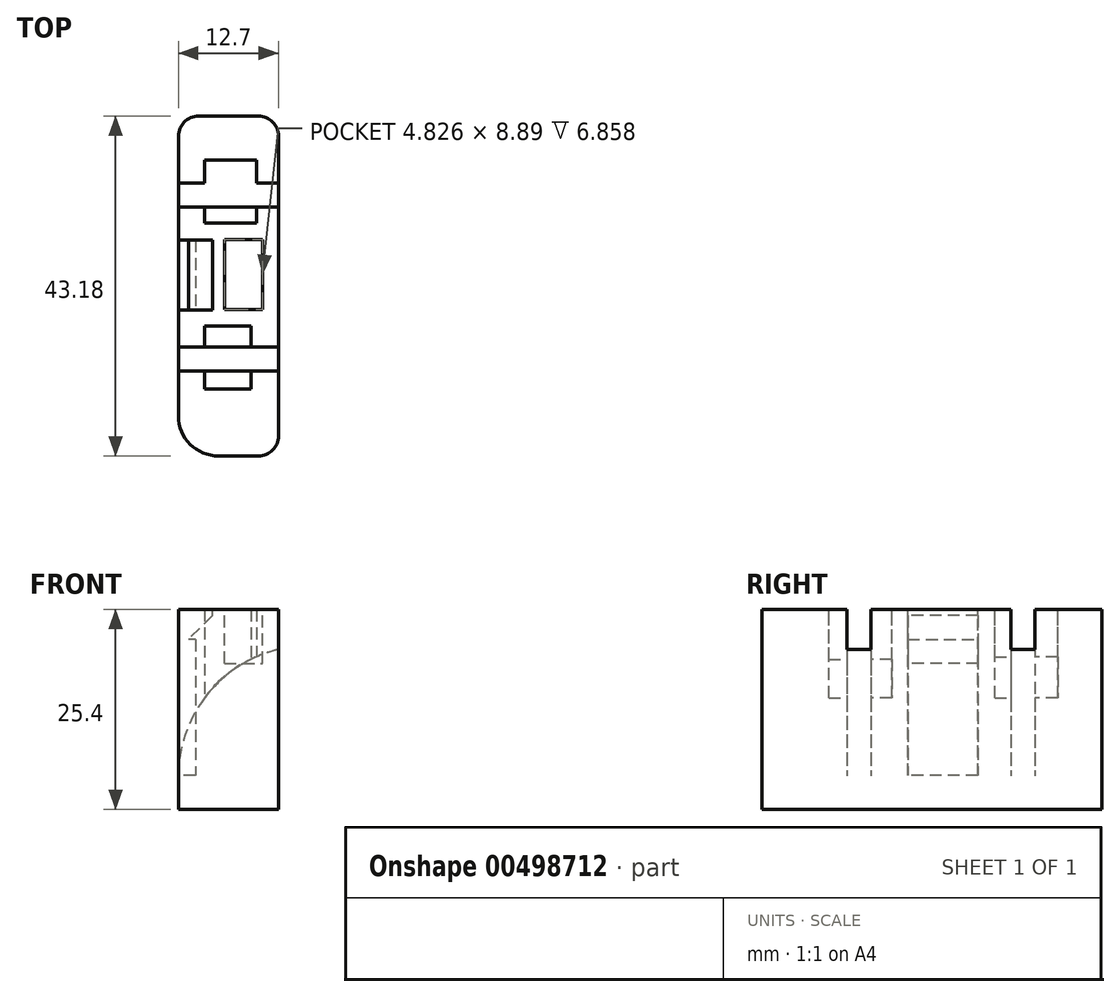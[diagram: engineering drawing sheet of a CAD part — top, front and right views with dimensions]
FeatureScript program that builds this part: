
annotation { "Feature Type Name" : "Feature", "Feature Type Description" : "" }
export const myFeature = defineFeature(function(context is Context, id is Id, definition is map)
    precondition{}
    {
        {
            var Q0;
            Q0=qCreatedBy(makeId("Top.planeOp"),FACE);
            var sketch = newSketch(context, id + "F0", { "sketchPlane" : qUnion([Q0])});
            skLineSegment(sketch, "E0.bottom", {"start": v(3.8, 21.6) * mm, "end": v(-3.81, 21.6) * mm});
            skLineSegment(sketch, "E0.top", {"start": v(3.8, -21.59) * mm, "end": v(-1.27, -21.59) * mm});
            skLineSegment(sketch, "E0.left", {"start": v(6.35, 19.05) * mm, "end": v(6.35, -19.05) * mm});
            skLineSegment(sketch, "E0.right", {"start": v(-6.35, 19.05) * mm, "end": v(-6.35, -16.51) * mm});
            skPoint(sketch, "E0.middle", {"position": v(0, 0) * mm});
            skPoint(sketch, "E1.visualSharp", {"position": v(6.35, 21.6) * mm});
            skArc(sketch, "E1.filletArc", {"start": v(6.35, 19.05) * mm, "mid": v(5.6, 20.85) * mm, "end": v(3.8, 21.6) * mm});
            skPoint(sketch, "E2.visualSharp", {"position": v(-6.35, 21.6) * mm});
            skArc(sketch, "E2.filletArc", {"start": v(-3.81, 21.59) * mm, "mid": v(-5.6, 20.85) * mm, "end": v(-6.35, 19.05) * mm});
            skPoint(sketch, "E3.visualSharp", {"position": v(6.35, -21.59) * mm});
            skArc(sketch, "E3.filletArc", {"start": v(3.8, -21.59) * mm, "mid": v(5.6, -20.85) * mm, "end": v(6.35, -19.05) * mm});
            skPoint(sketch, "E4.visualSharp", {"position": v(-6.35, -21.59) * mm});
            skArc(sketch, "E4.filletArc", {"start": v(-6.35, -16.51) * mm, "mid": v(-4.86, -20.1) * mm, "end": v(-1.27, -21.59) * mm});
            skSolve(sketch);
        }
        {
            var Q0;
            Q0 = qSketchRegion(id + "F0", true);
            extrude(context, id + "F1", {"entities" : qUnion([Q0]), "depth" : 25.4 * mm});
        }
        {
            var Q0;
            Q0=makeQuery(id+"F1.opExtrude","SWEPT_FACE",FACE,{"disambiguationData":[OSD([sQuery(id+"F0.wireOp",EDGE,"E0.left")])]});
            var sketch = newSketch(context, id + "F2", { "sketchPlane" : qUnion([Q0])});
            skLineSegment(sketch, "E5.bottom", {"start": v(-10.8, 25.4) * mm, "end": v(-7.75, 25.4) * mm});
            skLineSegment(sketch, "E5.top", {"start": v(-10.8, 20.32) * mm, "end": v(-7.75, 20.32) * mm});
            skLineSegment(sketch, "E5.left", {"start": v(-10.8, 25.4) * mm, "end": v(-10.8, 20.32) * mm});
            skLineSegment(sketch, "E5.right", {"start": v(-7.75, 25.4) * mm, "end": v(-7.75, 20.32) * mm});
            skLineSegment(sketch, "E6.bottom", {"start": v(10.03, 25.4) * mm, "end": v(13.08, 25.4) * mm});
            skLineSegment(sketch, "E6.top", {"start": v(10.03, 20.32) * mm, "end": v(13.08, 20.32) * mm});
            skLineSegment(sketch, "E6.left", {"start": v(10.03, 25.4) * mm, "end": v(10.03, 20.32) * mm});
            skLineSegment(sketch, "E6.right", {"start": v(13.08, 25.4) * mm, "end": v(13.08, 20.32) * mm});
            skSolve(sketch);
        }
        {
            var Q0;
            Q0=makeQuery(id+"F2.imprint","IMPRINT",FACE,{"disambiguationData":[TD([[makeQuery(id+"F2.imprint","IMPRINT",EDGE,{"derivedFrom":sQuery(id+"F2.wireOp",EDGE,"E5.bottom")}),1.0]])]});
            var Q1;
            Q1=makeQuery(id+"F2.imprint","IMPRINT",FACE,{"disambiguationData":[TD([[makeQuery(id+"F2.imprint","IMPRINT",EDGE,{"derivedFrom":sQuery(id+"F2.wireOp",EDGE,"E6.bottom")}),1.0]])]});
            extrude(context, id + "F3", {"entities" : qUnion([Q0, Q1]), "operationType" : NewBodyOperationType.REMOVE, "oppositeDirection" : true, "depth" : 15.24 * mm});
        }
        {
            var Q0;
            Q0=makeQuery(id+"F3.boolean.opBoolean","INTERSECT",EDGE,{"derivedFrom":[makeQuery(id+"F1.opExtrude","SWEPT_FACE",FACE,{"disambiguationData":[OSD([sQuery(id+"F0.wireOp",EDGE,"E0.right")])]}),makeQuery(id+"F3.opExtrude","SWEPT_FACE",FACE,{"disambiguationData":[OSD([sQuery(id+"F2.wireOp",EDGE,"E6.top")])]})]});
            fillet(context, id + "F4", {"entities" : qUnion([Q0]), "radius" : 16.5 * mm, "tangentPropagation" : true, "allowEdgeOverflow" : false});
        }
        {
            var Q0;
            Q0=makeQuery(id+"F3.boolean.opBoolean","INTERSECT",EDGE,{"derivedFrom":[makeQuery(id+"F1.opExtrude","SWEPT_FACE",FACE,{"disambiguationData":[OSD([sQuery(id+"F0.wireOp",EDGE,"E0.right")])]}),makeQuery(id+"F3.opExtrude","SWEPT_FACE",FACE,{"disambiguationData":[OSD([sQuery(id+"F2.wireOp",EDGE,"E5.top")])]})]});
            fillet(context, id + "F5", {"entities" : qUnion([Q0]), "radius" : 16.5 * mm, "tangentPropagation" : true, "allowEdgeOverflow" : false});
        }
        {
            var Q0;
            {var subQ0=sQuery(id+"F0.wireOp",EDGE,"E0.left");var subQ1=sQuery(id+"F0.wireOp",EDGE,"E0.right");Q0=makeQuery(id+"F3.boolean.opBoolean","SPLIT",FACE,{"disambiguationData":[TD([makeQuery(id+"F3.opExtrude","SWEPT_FACE",FACE,{"disambiguationData":[OSD([sQuery(id+"F2.wireOp",EDGE,"E5.right")])]})])],"derivedFrom":makeQuery(id+"F1.opExtrude","CAP_FACE",FACE,{"disambiguationData":[OSD([sQuery(id+"F0.wireOp",EDGE,"E0.bottom"),sQuery(id+"F0.wireOp",EDGE,"E0.top"),subQ0,subQ1,sQuery(id+"F0.wireOp",EDGE,"E1.filletArc"),sQuery(id+"F0.wireOp",EDGE,"E2.filletArc"),sQuery(id+"F0.wireOp",EDGE,"E3.filletArc"),sQuery(id+"F0.wireOp",EDGE,"E4.filletArc")])],"isStart":false})});}
            var sketch = newSketch(context, id + "F6", { "sketchPlane" : qUnion([Q0])});
            skLineSegment(sketch, "E7.bottom", {"start": v(-3.05, -5.08) * mm, "end": v(2.9, -5.08) * mm});
            skLineSegment(sketch, "E7.top", {"start": v(-3.05, -13.08) * mm, "end": v(2.9, -13.08) * mm});
            skLineSegment(sketch, "E7.left", {"start": v(-3.05, -5.08) * mm, "end": v(-3.05, -13.08) * mm});
            skLineSegment(sketch, "E7.right", {"start": v(2.9, -5.08) * mm, "end": v(2.9, -13.08) * mm});
            skLineSegment(sketch, "E8.bottom", {"start": v(-3.05, 16) * mm, "end": v(3.54, 16) * mm});
            skLineSegment(sketch, "E8.top", {"start": v(-3.05, 8) * mm, "end": v(3.54, 8) * mm});
            skLineSegment(sketch, "E8.left", {"start": v(-3.05, 16) * mm, "end": v(-3.05, 8) * mm});
            skLineSegment(sketch, "E8.right", {"start": v(3.54, 16) * mm, "end": v(3.54, 8) * mm});
            skSolve(sketch);
        }
        {
            var Q0;
            {var subQ0=sQuery(id+"F6.wireOp",EDGE,"E8.bottom");Q0=makeQuery(id+"F6.imprint","IMPRINT",FACE,{"disambiguationData":[TD([[makeQuery(id+"F6.imprint","IMPRINT",EDGE,{"derivedFrom":subQ0}),-1.0]])]});}
            var Q1;
            {var subQ0=sQuery(id+"F6.wireOp",EDGE,"E8.top");Q1=makeQuery(id+"F6.imprint","IMPRINT",FACE,{"disambiguationData":[TD([[makeQuery(id+"F6.imprint","IMPRINT",EDGE,{"derivedFrom":subQ0}),1.0]])]});}
            var Q2;
            {var subQ0=sQuery(id+"F6.wireOp",EDGE,"E7.bottom");Q2=makeQuery(id+"F6.imprint","IMPRINT",FACE,{"disambiguationData":[TD([[makeQuery(id+"F6.imprint","IMPRINT",EDGE,{"derivedFrom":subQ0}),-1.0]])]});}
            var Q3;
            {var subQ0=sQuery(id+"F6.wireOp",EDGE,"E7.top");Q3=makeQuery(id+"F6.imprint","IMPRINT",FACE,{"disambiguationData":[TD([[makeQuery(id+"F6.imprint","IMPRINT",EDGE,{"derivedFrom":subQ0}),1.0]])]});}
            extrude(context, id + "F7", {"entities" : qUnion([Q0, Q1, Q2, Q3]), "operationType" : NewBodyOperationType.REMOVE, "oppositeDirection" : true, "depth" : 5.6 * mm});
        }
        {
            var Q0;
            Q0=makeQuery(id+"F3.boolean.opBoolean","COPY",FACE,{"derivedFrom":makeQuery(id+"F3.opExtrude","SWEPT_FACE",FACE,{"disambiguationData":[OSD([sQuery(id+"F2.wireOp",EDGE,"E5.left")])]})});
            var sketch = newSketch(context, id + "F8", { "sketchPlane" : qUnion([Q0])});
            skLineSegment(sketch, "E9", {"start": v(-2.9, 19.81) * mm, "end": v(-2.9, 19.08) * mm});
            skLineSegment(sketch, "E10", {"start": v(3.05, 19.81) * mm, "end": v(3.05, 14.16) * mm});
            skLineSegment(sketch, "E11", {"start": v(-2.9, 19.81) * mm, "end": v(3.05, 19.81) * mm});
            skArc(sketch, "E12", {"start": v(3.05, 14.16) * mm, "mid": v(0.38, 16.99) * mm, "end": v(-2.9, 19.08) * mm});
            skSolve(sketch);
        }
        {
            var Q0;
            Q0=makeQuery(id+"F8.imprint","IMPRINT",FACE,{"disambiguationData":[TD([[makeQuery(id+"F8.imprint","IMPRINT",EDGE,{"derivedFrom":sQuery(id+"F8.wireOp",EDGE,"E9")}),1.0]])]});
            extrude(context, id + "F9", {"entities" : qUnion([Q0]), "operationType" : NewBodyOperationType.REMOVE, "oppositeDirection" : true, "depth" : 2.3 * mm});
        }
        {
            var Q0;
            Q0=makeQuery(id+"F3.boolean.opBoolean","COPY",FACE,{"derivedFrom":makeQuery(id+"F3.opExtrude","SWEPT_FACE",FACE,{"disambiguationData":[OSD([sQuery(id+"F2.wireOp",EDGE,"E5.right")])]})});
            var sketch = newSketch(context, id + "F10", { "sketchPlane" : qUnion([Q0])});
            skLineSegment(sketch, "E13", {"start": v(2.9, 19.81) * mm, "end": v(2.9, 19.08) * mm});
            skLineSegment(sketch, "E14", {"start": v(-3.05, 19.81) * mm, "end": v(-3.05, 14.16) * mm});
            skLineSegment(sketch, "E15", {"start": v(-3.05, 19.81) * mm, "end": v(2.9, 19.81) * mm});
            skArc(sketch, "E16", {"start": v(2.9, 19.08) * mm, "mid": v(-0.38, 16.99) * mm, "end": v(-3.05, 14.16) * mm});
            skSolve(sketch);
        }
        {
            var Q0;
            Q0=makeQuery(id+"F10.imprint","IMPRINT",FACE,{"disambiguationData":[TD([[makeQuery(id+"F10.imprint","IMPRINT",EDGE,{"derivedFrom":sQuery(id+"F10.wireOp",EDGE,"E13")}),-1.0]])]});
            extrude(context, id + "F11", {"entities" : qUnion([Q0]), "operationType" : NewBodyOperationType.REMOVE, "oppositeDirection" : true, "depth" : 2.67 * mm});
        }
        {
            var Q0;
            Q0=makeQuery(id+"F3.boolean.opBoolean","COPY",FACE,{"derivedFrom":makeQuery(id+"F3.opExtrude","SWEPT_FACE",FACE,{"disambiguationData":[OSD([sQuery(id+"F2.wireOp",EDGE,"E6.right")])]})});
            var sketch = newSketch(context, id + "F12", { "sketchPlane" : qUnion([Q0])});
            skLineSegment(sketch, "E17", {"start": v(3.54, 19.81) * mm, "end": v(3.54, 19.38) * mm});
            skLineSegment(sketch, "E18", {"start": v(3.54, 19.81) * mm, "end": v(-3.05, 19.81) * mm});
            skPoint(sketch, "E19.endSnap0", {"position": v(-2.8, 14.5) * mm});
            skLineSegment(sketch, "E20", {"start": v(-3.05, 19.81) * mm, "end": v(-3.05, 14.16) * mm});
            skArc(sketch, "E21", {"start": v(3.54, 19.38) * mm, "mid": v(-0.08, 17.19) * mm, "end": v(-3.05, 14.16) * mm});
            skSolve(sketch);
        }
        {
            var Q0;
            {var subQ0=sQuery(id+"F12.wireOp",EDGE,"E17");Q0=makeQuery(id+"F12.imprint","IMPRINT",FACE,{"disambiguationData":[TD([[makeQuery(id+"F12.imprint","IMPRINT",EDGE,{"derivedFrom":subQ0}),-1.0]])]});}
            extrude(context, id + "F13", {"entities" : qUnion([Q0]), "operationType" : NewBodyOperationType.REMOVE, "oppositeDirection" : true, "depth" : 2.92 * mm});
        }
        {
            var Q0;
            Q0=makeQuery(id+"F3.boolean.opBoolean","COPY",FACE,{"derivedFrom":makeQuery(id+"F3.opExtrude","SWEPT_FACE",FACE,{"disambiguationData":[OSD([sQuery(id+"F2.wireOp",EDGE,"E6.left")])]})});
            var sketch = newSketch(context, id + "F14", { "sketchPlane" : qUnion([Q0])});
            skLineSegment(sketch, "E22", {"start": v(3.05, 19.81) * mm, "end": v(-3.54, 19.81) * mm});
            skLineSegment(sketch, "E23", {"start": v(-3.54, 19.81) * mm, "end": v(-3.54, 19.38) * mm});
            skLineSegment(sketch, "E24", {"start": v(3.05, 19.81) * mm, "end": v(3.05, 14.16) * mm});
            skArc(sketch, "E25", {"start": v(3.05, 14.16) * mm, "mid": v(0.1, 17.21) * mm, "end": v(-3.54, 19.38) * mm});
            skSolve(sketch);
        }
        {
            var Q0;
            Q0=makeQuery(id+"F14.imprint","IMPRINT",FACE,{"disambiguationData":[TD([[makeQuery(id+"F14.imprint","IMPRINT",EDGE,{"derivedFrom":sQuery(id+"F14.wireOp",EDGE,"E22")}),-1.0]])]});
            extrude(context, id + "F15", {"entities" : qUnion([Q0]), "operationType" : NewBodyOperationType.REMOVE, "oppositeDirection" : true, "depth" : 2.03 * mm});
        }
        {
            var Q0;
            {var subQ0=sQuery(id+"F0.wireOp",EDGE,"E0.left");var subQ1=sQuery(id+"F0.wireOp",EDGE,"E0.right");Q0=makeQuery(id+"F3.boolean.opBoolean","SPLIT",FACE,{"disambiguationData":[TD([makeQuery(id+"F3.opExtrude","SWEPT_FACE",FACE,{"disambiguationData":[OSD([sQuery(id+"F2.wireOp",EDGE,"E5.right")])]})])],"derivedFrom":makeQuery(id+"F1.opExtrude","CAP_FACE",FACE,{"disambiguationData":[OSD([sQuery(id+"F0.wireOp",EDGE,"E0.bottom"),sQuery(id+"F0.wireOp",EDGE,"E0.top"),subQ0,subQ1,sQuery(id+"F0.wireOp",EDGE,"E1.filletArc"),sQuery(id+"F0.wireOp",EDGE,"E2.filletArc"),sQuery(id+"F0.wireOp",EDGE,"E3.filletArc"),sQuery(id+"F0.wireOp",EDGE,"E4.filletArc")])],"isStart":false})});}
            var sketch = newSketch(context, id + "F16", { "sketchPlane" : qUnion([Q0])});
            skLineSegment(sketch, "E26.bottom", {"start": v(-0.5, 5.9) * mm, "end": v(4.32, 5.9) * mm});
            skLineSegment(sketch, "E26.top", {"start": v(-0.5, -2.98) * mm, "end": v(4.32, -2.98) * mm});
            skLineSegment(sketch, "E26.left", {"start": v(-0.5, 5.9) * mm, "end": v(-0.5, -2.98) * mm});
            skLineSegment(sketch, "E26.right", {"start": v(4.32, 5.9) * mm, "end": v(4.32, -2.98) * mm});
            skSolve(sketch);
        }
        {
            var Q0;
            Q0=makeQuery(id+"F16.imprint","IMPRINT",FACE,{"disambiguationData":[TD([[makeQuery(id+"F16.imprint","IMPRINT",EDGE,{"derivedFrom":sQuery(id+"F16.wireOp",EDGE,"E26.bottom")}),-1.0]])]});
            extrude(context, id + "F17", {"entities" : qUnion([Q0]), "operationType" : NewBodyOperationType.REMOVE, "oppositeDirection" : true, "depth" : 6.86 * mm});
        }
        {
            var Q0;
            {var subQ0=sQuery(id+"F0.wireOp",EDGE,"E0.left");var subQ1=sQuery(id+"F0.wireOp",EDGE,"E0.right");Q0=makeQuery(id+"F3.boolean.opBoolean","SPLIT",FACE,{"disambiguationData":[TD([makeQuery(id+"F3.opExtrude","SWEPT_FACE",FACE,{"disambiguationData":[OSD([sQuery(id+"F2.wireOp",EDGE,"E5.right")])]})])],"derivedFrom":makeQuery(id+"F1.opExtrude","CAP_FACE",FACE,{"disambiguationData":[OSD([sQuery(id+"F0.wireOp",EDGE,"E0.bottom"),sQuery(id+"F0.wireOp",EDGE,"E0.top"),subQ0,subQ1,sQuery(id+"F0.wireOp",EDGE,"E1.filletArc"),sQuery(id+"F0.wireOp",EDGE,"E2.filletArc"),sQuery(id+"F0.wireOp",EDGE,"E3.filletArc"),sQuery(id+"F0.wireOp",EDGE,"E4.filletArc")])],"isStart":false})});}
            var sketch = newSketch(context, id + "F18", { "sketchPlane" : qUnion([Q0])});
            skLineSegment(sketch, "E27.bottom", {"start": v(-6.35, 5.84) * mm, "end": v(-2.03, 5.84) * mm});
            skLineSegment(sketch, "E27.top", {"start": v(-6.35, -3.05) * mm, "end": v(-2.03, -3.05) * mm});
            skLineSegment(sketch, "E27.left", {"start": v(-6.35, 5.84) * mm, "end": v(-6.35, -3.05) * mm});
            skLineSegment(sketch, "E27.right", {"start": v(-2.03, 5.84) * mm, "end": v(-2.03, -3.05) * mm});
            skSolve(sketch);
        }
        {
            var Q0;
            Q0=makeQuery(id+"F18.imprint","IMPRINT",FACE,{"disambiguationData":[TD([[makeQuery(id+"F18.imprint","IMPRINT",EDGE,{"derivedFrom":sQuery(id+"F18.wireOp",EDGE,"E27.bottom")}),-1.0]])]});
            extrude(context, id + "F19", {"entities" : qUnion([Q0]), "operationType" : NewBodyOperationType.REMOVE, "oppositeDirection" : true, "depth" : 3.8 * mm});
        }
        {
            var Q0;
            Q0=makeQuery(id+"F19.boolean.opBoolean","COPY",EDGE,{"derivedFrom":makeQuery(id+"F19.opExtrude","CAP_EDGE",EDGE,{"disambiguationData":[OSD([sQuery(id+"F18.wireOp",EDGE,"E27.right")])],"isStart":false})});
            chamfer(context, id + "F20", {"entities" : qUnion([Q0]), "width" : 3.05 * mm, "tangentPropagation" : true});
        }
        {
            var Q0;
            Q0=makeQuery(id+"F1.opExtrude","SWEPT_FACE",FACE,{"disambiguationData":[OSD([sQuery(id+"F0.wireOp",EDGE,"E0.right")])]});
            var sketch = newSketch(context, id + "F21", { "sketchPlane" : qUnion([Q0])});
            skLineSegment(sketch, "E28.bottom", {"start": v(-5.84, 21.59) * mm, "end": v(3.05, 21.59) * mm});
            skLineSegment(sketch, "E28.top", {"start": v(-5.84, 4.32) * mm, "end": v(3.05, 4.32) * mm});
            skLineSegment(sketch, "E28.left", {"start": v(-5.84, 21.59) * mm, "end": v(-5.84, 4.32) * mm});
            skLineSegment(sketch, "E28.right", {"start": v(3.05, 21.59) * mm, "end": v(3.05, 4.32) * mm});
            skSolve(sketch);
        }
        {
            var Q0;
            Q0=makeQuery(id+"F21.imprint","IMPRINT",FACE,{"disambiguationData":[TD([[makeQuery(id+"F21.imprint","IMPRINT",EDGE,{"derivedFrom":sQuery(id+"F21.wireOp",EDGE,"E28.bottom")}),-1.0]])]});
            extrude(context, id + "F22", {"entities" : qUnion([Q0]), "operationType" : NewBodyOperationType.REMOVE, "oppositeDirection" : true, "depth" : 2.16 * mm});
        }
    });
